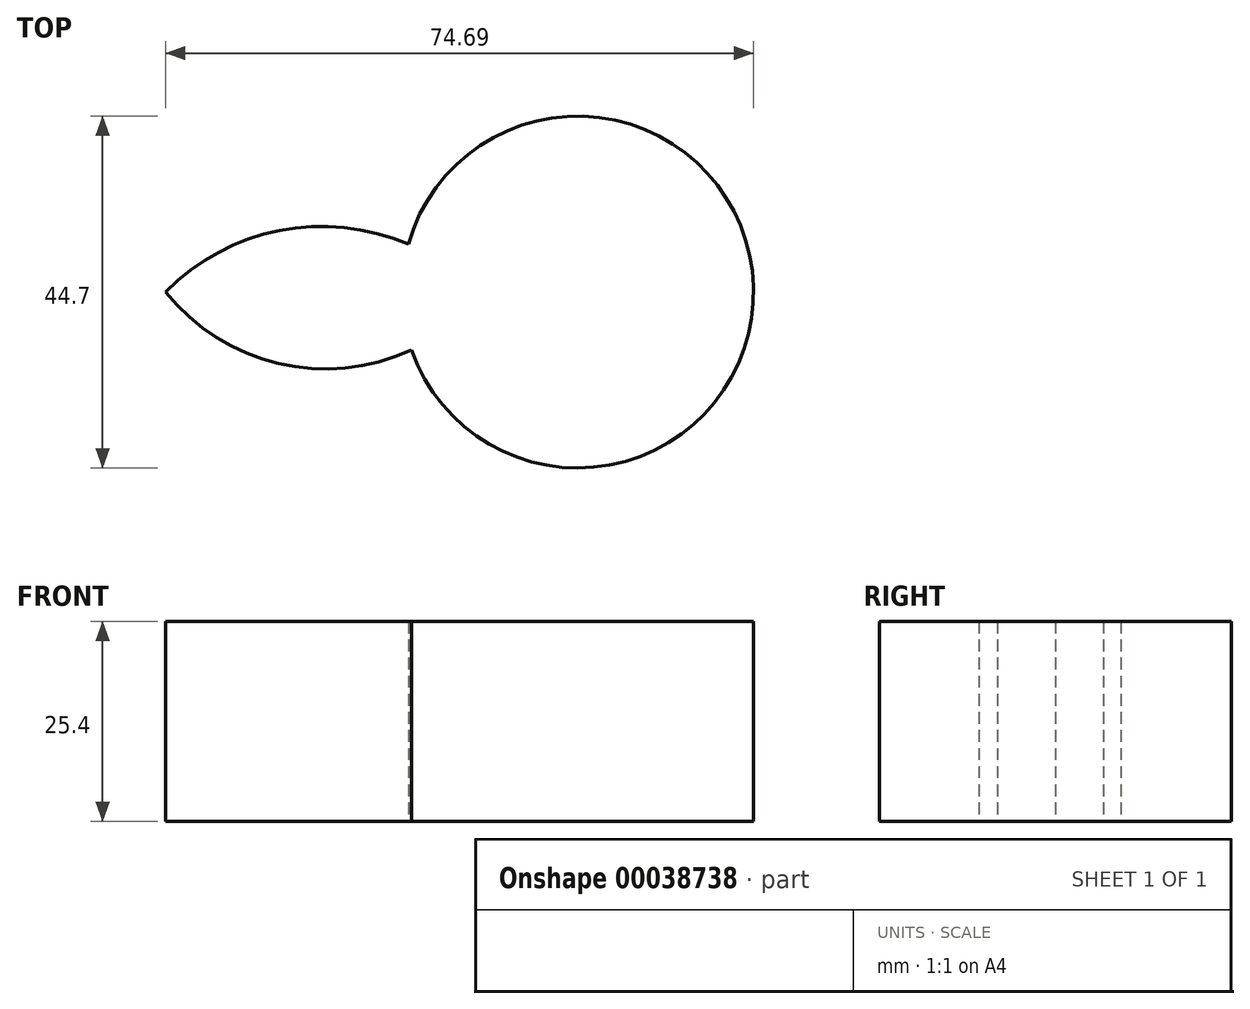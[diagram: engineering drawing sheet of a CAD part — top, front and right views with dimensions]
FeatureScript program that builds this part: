
annotation { "Feature Type Name" : "Feature", "Feature Type Description" : "" }
export const myFeature = defineFeature(function(context is Context, id is Id, definition is map)
    precondition{}
    {
        {
            var Q0;
            Q0=qCreatedBy(makeId("Top.planeOp"),FACE);
            var sketch = newSketch(context, id + "F0", { "sketchPlane" : qUnion([Q0])});
            skLineSegment(sketch, "E0", {"start": v(0, 0) * mm, "end": v(0, 75.55) * mm});
            skLineSegment(sketch, "E1", {"start": v(0, 75.55) * mm, "end": v(0, -76.13) * mm});
            skCircle(sketch, "E2", {"center": v(0, 0) * mm, "radius": 22.35 * mm});
            skArc(sketch, "E3", {"start": v(-52.34, 0) * mm, "mid": v(-37.99, -9.06) * mm, "end": v(-21.1, -7.35) * mm});
            skArc(sketch, "E4", {"start": v(-21.5, 6.08) * mm, "mid": v(-37.86, 7.8) * mm, "end": v(-52.34, 0) * mm});
            skSolve(sketch);
        }
        {
            var Q0;
            Q0=sQuery(id+"F0.wireOp",EDGE,"E4");
            var Q1;
            Q1=sQuery(id+"F0.wireOp",EDGE,"E3");
            extrude(context, id + "F1", {"bodyType" : ToolBodyType.SURFACE, "surfaceEntities" : qUnion([Q0, Q1]), "depth" : 25.4 * mm});
        }
        {
            var Q0;
            Q0 = qSketchRegion(id + "F0", true);
            extrude(context, id + "F2", {"entities" : qUnion([Q0]), "depth" : 25.4 * mm});
        }
    });
